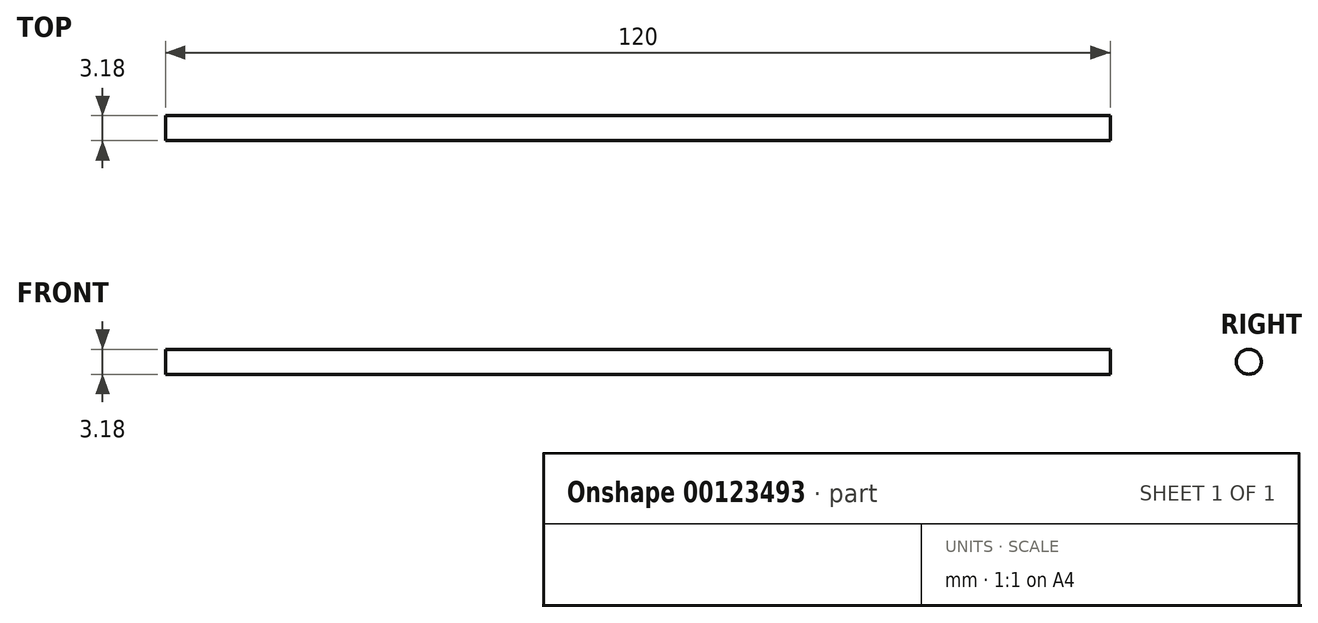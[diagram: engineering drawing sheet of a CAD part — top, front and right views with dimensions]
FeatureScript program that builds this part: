
annotation { "Feature Type Name" : "Feature", "Feature Type Description" : "" }
export const myFeature = defineFeature(function(context is Context, id is Id, definition is map)
    precondition{}
    {
        {
            var Q0;
            Q0=qCreatedBy(makeId("Right.planeOp"),FACE);
            var sketch = newSketch(context, id + "F0", { "sketchPlane" : qUnion([Q0])});
            skCircle(sketch, "E0", {"center": v(0, 0) * mm, "radius": 1.59 * mm});
            skSolve(sketch);
        }
        {
            var Q0;
            Q0 = qSketchRegion(id + "F0", true);
            extrude(context, id + "F1", {"entities" : qUnion([Q0]), "depth" : 120 * mm});
        }
    });
